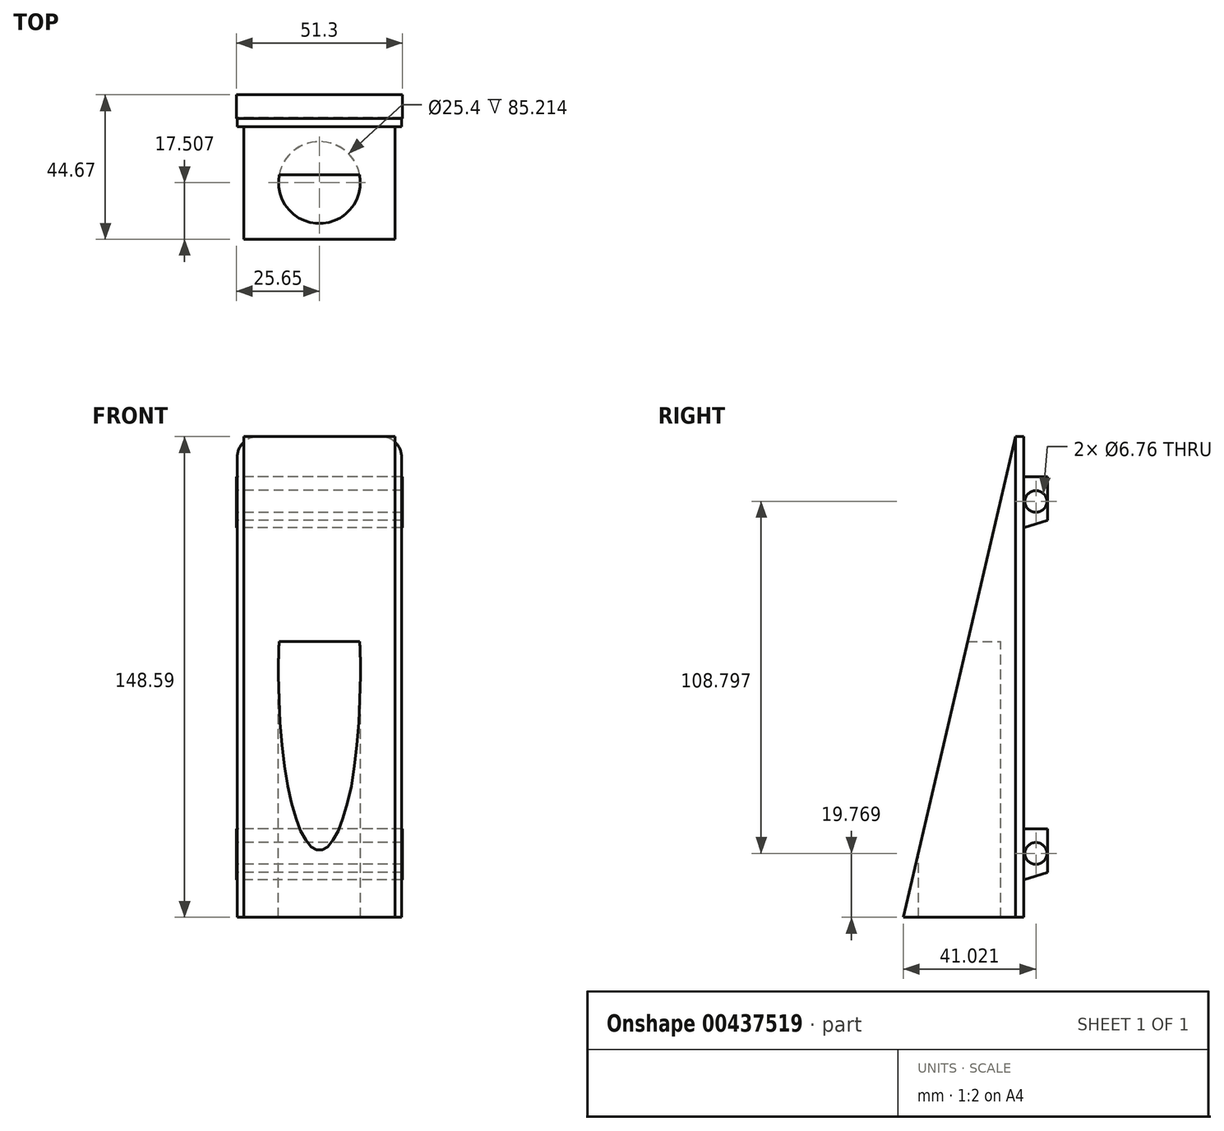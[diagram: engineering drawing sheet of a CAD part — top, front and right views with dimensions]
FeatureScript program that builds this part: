
annotation { "Feature Type Name" : "Feature", "Feature Type Description" : "" }
export const myFeature = defineFeature(function(context is Context, id is Id, definition is map)
    precondition{}
    {
        {
            var Q0;
            Q0=qCreatedBy(makeId("Front.planeOp"),FACE);
            var sketch = newSketch(context, id + "F0", { "sketchPlane" : qUnion([Q0])});
            skLineSegment(sketch, "E0", {"start": v(0, 63.38) * mm, "end": v(-19.05, 63.38) * mm});
            skLineSegment(sketch, "E1", {"start": v(-25.4, 57.03) * mm, "end": v(-25.4, -85.21) * mm});
            skLineSegment(sketch, "E2", {"start": v(-25.4, -85.21) * mm, "end": v(0, -85.21) * mm});
            skPoint(sketch, "E3.visualSharp", {"position": v(-25.4, 63.38) * mm});
            skArc(sketch, "E3.filletArc", {"start": v(-19.05, 63.38) * mm, "mid": v(-23.54, 61.52) * mm, "end": v(-25.4, 57.03) * mm});
            skLineSegment(sketch, "E4", {"start": v(0, 75.68) * mm, "end": v(0, -104.38) * mm});
            skLineSegment(sketch, "E5.MirrorCS", {"start": v(0, 63.38) * mm, "end": v(19.05, 63.38) * mm});
            skPoint(sketch, "E6.MirrorP", {"position": v(25.4, 63.38) * mm});
            skArc(sketch, "E7.MirrorCS", {"start": v(19.05, 63.38) * mm, "mid": v(23.54, 61.52) * mm, "end": v(25.4, 57.03) * mm});
            skLineSegment(sketch, "E8.MirrorCS", {"start": v(25.4, 57.03) * mm, "end": v(25.4, -85.21) * mm});
            skLineSegment(sketch, "E9.MirrorCS", {"start": v(25.4, -85.21) * mm, "end": v(0, -85.21) * mm});
            skSolve(sketch);
        }
        {
            var Q0;
            Q0 = qSketchRegion(id + "F0", true);
            extrude(context, id + "F1", {"entities" : qUnion([Q0]), "depth" : 2.54 * mm});
        }
        {
            var Q0;
            Q0=qCreatedBy(makeId("Right.planeOp"),FACE);
            var sketch = newSketch(context, id + "F2", { "sketchPlane" : qUnion([Q0])});
            skLineSegment(sketch, "E10", {"start": v(-2.54, 63.38) * mm, "end": v(-2.54, -85.21) * mm});
            skLineSegment(sketch, "E11", {"start": v(-2.54, -85.21) * mm, "end": v(-37.33, -85.21) * mm});
            skLineSegment(sketch, "E12", {"start": v(-37.33, -85.21) * mm, "end": v(-2.54, 63.38) * mm});
            skSolve(sketch);
        }
        {
            var Q0;
            Q0=qCreatedBy(makeId("Right.planeOp"),FACE);
            var sketch = newSketch(context, id + "F3", { "sketchPlane" : qUnion([Q0])});
            skCircle(sketch, "E13", {"center": v(21.82, -96.36) * mm, "radius": 3.31 * mm});
            skCircle(sketch, "E14", {"center": v(22.9, -52.47) * mm, "radius": 3.31 * mm});
            skSolve(sketch);
        }
        {
            var Q0;
            Q0 = qSketchRegion(id + "F3", true);
            extrude(context, id + "F4", {"entities" : qUnion([Q0]), "endBound" : BoundingType.SYMMETRIC, "depth" : 68.83 * mm});
        }
        {
            var Q0;
            Q0=qCreatedBy(makeId("Right.planeOp"),FACE);
            var sketch = newSketch(context, id + "F5", { "sketchPlane" : qUnion([Q0])});
            skCircle(sketch, "E15", {"center": v(38.59, -76.95) * mm, "radius": 6.35 * mm});
            skCircle(sketch, "E16", {"center": v(38.59, -76.95) * mm, "radius": 3.31 * mm});
            skCircle(sketch, "E17", {"center": v(51.06, -64.86) * mm, "radius": 6.35 * mm});
            skCircle(sketch, "E18", {"center": v(51.06, -64.86) * mm, "radius": 3.31 * mm});
            skCircle(sketch, "E19", {"center": v(20.48, -4) * mm, "radius": 6.35 * mm});
            skCircle(sketch, "E20", {"center": v(20.48, -4) * mm, "radius": 3.31 * mm});
            skCircle(sketch, "E21", {"center": v(29.17, 27.4) * mm, "radius": 6.35 * mm});
            skCircle(sketch, "E22", {"center": v(29.17, 27.4) * mm, "radius": 3.31 * mm});
            skSolve(sketch);
        }
        {
            var Q0;
            Q0 = qSketchRegion(id + "F5", true);
            extrude(context, id + "F6", {"entities" : qUnion([Q0]), "depth" : 8.9 * mm});
        }
        {
            var Q0;
            Q0 = qSketchRegion(id + "F2", true);
            extrude(context, id + "F7", {"entities" : qUnion([Q0]), "operationType" : NewBodyOperationType.ADD, "endBound" : BoundingType.SYMMETRIC, "depth" : 46.74 * mm});
        }
        {
            var Q0;
            Q0=qCreatedBy(makeId("Right.planeOp"),FACE);
            var sketch = newSketch(context, id + "F8", { "sketchPlane" : qUnion([Q0])});
            skCircle(sketch, "E23", {"center": v(3.7, -65.44) * mm, "radius": 3.38 * mm});
            skLineSegment(sketch, "E24", {"start": v(0, -68.1) * mm, "end": v(0, -57.81) * mm});
            skLineSegment(sketch, "E25", {"start": v(0, -57.81) * mm, "end": v(7.34, -57.81) * mm});
            skLineSegment(sketch, "E26", {"start": v(0, -73.59) * mm, "end": v(7.34, -71.28) * mm});
            skLineSegment(sketch, "E27", {"start": v(7.34, -71.28) * mm, "end": v(7.34, -57.81) * mm});
            skLineSegment(sketch, "E28", {"start": v(0, -68.1) * mm, "end": v(0, -73.59) * mm});
            skCircle(sketch, "E29", {"center": v(3.7, 43.36) * mm, "radius": 3.38 * mm});
            skLineSegment(sketch, "E30", {"start": v(0, 40.7) * mm, "end": v(0, 50.99) * mm});
            skLineSegment(sketch, "E31", {"start": v(0, 50.99) * mm, "end": v(7.34, 50.99) * mm});
            skLineSegment(sketch, "E32", {"start": v(0, 35.2) * mm, "end": v(7.34, 37.52) * mm});
            skLineSegment(sketch, "E33", {"start": v(7.34, 37.52) * mm, "end": v(7.34, 50.99) * mm});
            skLineSegment(sketch, "E34", {"start": v(0, 40.7) * mm, "end": v(0, 35.2) * mm});
            skSolve(sketch);
        }
        {
            var Q0;
            Q0 = qSketchRegion(id + "F8", true);
            extrude(context, id + "F9", {"entities" : qUnion([Q0]), "operationType" : NewBodyOperationType.ADD, "endBound" : BoundingType.SYMMETRIC, "depth" : 51.3 * mm});
        }
        {
            var Q0;
            Q0=qCreatedBy(makeId("Top.planeOp"),FACE);
            var sketch = newSketch(context, id + "F10", { "sketchPlane" : qUnion([Q0])});
            skCircle(sketch, "E35", {"center": v(0, -19.82) * mm, "radius": 12.7 * mm});
            skSolve(sketch);
        }
        {
            var Q0;
            Q0 = qSketchRegion(id + "F10", true);
            extrude(context, id + "F11", {"entities" : qUnion([Q0]), "operationType" : NewBodyOperationType.REMOVE, "oppositeDirection" : true, "depth" : 102.87 * mm});
        }
        {
            var Q0;
            Q0=makeQuery(id+"F4.opExtrude","SWEPT_BODY",BODY,{"disambiguationData":[OSD([sQuery(id+"F3.wireOp",EDGE,"E13")])]});
            var Q1;
            Q1=makeQuery(id+"F6.opExtrude","SWEPT_BODY",BODY,{"disambiguationData":[OSD([sQuery(id+"F5.wireOp",EDGE,"E21"),sQuery(id+"F5.wireOp",EDGE,"E22")])]});
            var Q2;
            Q2=makeQuery(id+"F6.opExtrude","SWEPT_BODY",BODY,{"disambiguationData":[OSD([sQuery(id+"F5.wireOp",EDGE,"E19"),sQuery(id+"F5.wireOp",EDGE,"E20")])]});
            var Q3;
            Q3=makeQuery(id+"F6.opExtrude","SWEPT_BODY",BODY,{"disambiguationData":[OSD([sQuery(id+"F5.wireOp",EDGE,"E17"),sQuery(id+"F5.wireOp",EDGE,"E18")])]});
            var Q4;
            Q4=makeQuery(id+"F6.opExtrude","SWEPT_BODY",BODY,{"disambiguationData":[OSD([sQuery(id+"F5.wireOp",EDGE,"E15"),sQuery(id+"F5.wireOp",EDGE,"E16")])]});
            var Q5;
            Q5=makeQuery(id+"F4.opExtrude","SWEPT_BODY",BODY,{"disambiguationData":[OSD([sQuery(id+"F3.wireOp",EDGE,"E14")])]});
            deleteBodies(context, id + "F12", {"entities" : qUnion([Q0, Q1, Q2, Q3, Q4, Q5])});
        }
    });
